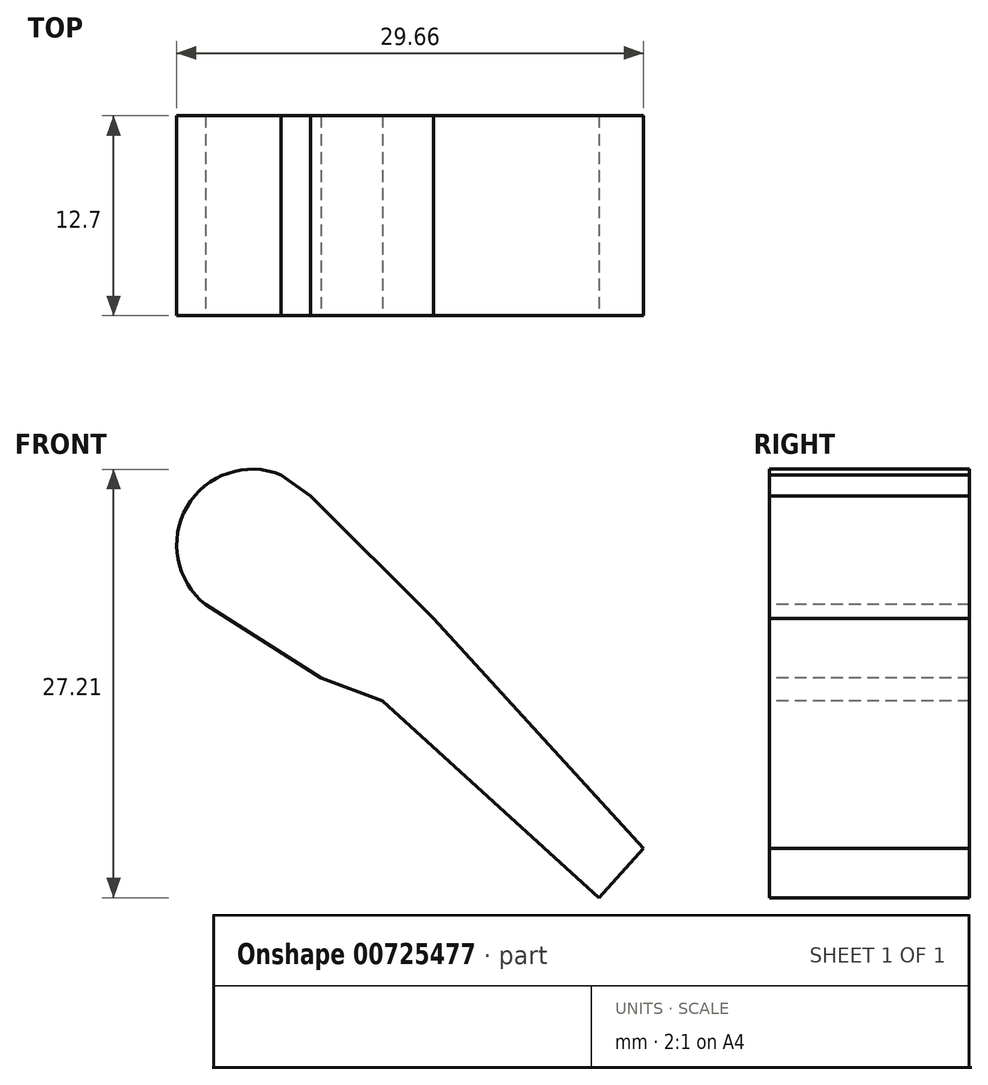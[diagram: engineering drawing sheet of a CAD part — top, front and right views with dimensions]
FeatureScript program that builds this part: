
annotation { "Feature Type Name" : "Feature", "Feature Type Description" : "" }
export const myFeature = defineFeature(function(context is Context, id is Id, definition is map)
    precondition{}
    {
        {
            var Q0;
            Q0=qCreatedBy(makeId("Front.planeOp"),FACE);
            var sketch = newSketch(context, id + "F0", { "sketchPlane" : qUnion([Q0])});
            skArc(sketch, "E0", {"start": v(-7.94, 72.96) * mm, "mid": v(-13.9, 70.92) * mm, "end": v(-12.72, 64.73) * mm});
            skLineSegment(sketch, "E1", {"start": v(-12.72, 64.73) * mm, "end": v(-5.38, 60.05) * mm});
            skLineSegment(sketch, "E2", {"start": v(-5.38, 60.05) * mm, "end": v(-1.48, 58.6) * mm});
            skLineSegment(sketch, "E3", {"start": v(-1.48, 58.6) * mm, "end": v(1.74, 63.84) * mm});
            skLineSegment(sketch, "E4", {"start": v(1.74, 63.84) * mm, "end": v(-6.05, 71.61) * mm});
            skLineSegment(sketch, "E5", {"start": v(-6.05, 71.61) * mm, "end": v(-7.94, 72.96) * mm});
            skLineSegment(sketch, "E6", {"start": v(12.25, 46.1) * mm, "end": v(15.1, 49.22) * mm});
            skLineSegment(sketch, "E7", {"start": v(15.1, 49.22) * mm, "end": v(1.74, 63.84) * mm});
            skLineSegment(sketch, "E8", {"start": v(-1.48, 58.6) * mm, "end": v(12.25, 46.1) * mm});
            skSolve(sketch);
        }
        {
            var Q0;
            Q0 = qSketchRegion(id + "F0", true);
            extrude(context, id + "F1", {"entities" : qUnion([Q0]), "oppositeDirection" : true, "depth" : 12.7 * mm, "offsetDistance" : 25.4 * mm});
        }
    });
